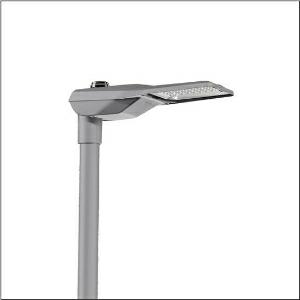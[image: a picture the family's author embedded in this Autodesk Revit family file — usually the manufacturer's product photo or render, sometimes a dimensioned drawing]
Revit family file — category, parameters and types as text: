
# Revit family: streetlight_sl_21_mini___p0_8a_5xe6u47n08hb_863c
name_source: partatom
category: Lighting Fixtures
units: mm (PartAtom-declared; Revit-internal decimal feet)

## family parameters
Cut with Voids When Loaded = No
Host = Face
Light Source = No
Part Type = Normal
Room Calculation Point = No
Round Connector Dimension = Use Diameter
Shared = No

## types (1)
- --- (1 x LED, 9510 lm, 66 W, 4000K)
    Apparent Load = 66 VA
    CIE Flux Codes = 33 69 96 100 100
    Color Rendering = 70
    Color Temperature = 4000K
    Default Elevation = 1800 mm
    Description = Streetlight SL 21 mini, mast luminaire, primary light control with lens, of PMMA, primary optical cover: cover, of toughened safety glass, transparent, light distribution: P0.8a, light emission: direct distribution, primary light characteristic: asymmetric, installation type: side-entry, LED, 3G 1.5mm², High Power LED, rated luminous flux: 9.510lm, luminous efficacy: 144lm/W, light colour: 740, colour temperature: 4000K, control gear: NEMA (7pin), control: flexible luminous flux parameterisation, time-dependent luminous flux control, constant luminous flux control, pre-setting: linear dimming characteristic, overheat protection, mains connection: 230..240V, AC, 50/60Hz, connection cable pre-assembled, cable length: 8,5m, wiring characteristics: H07RN-F, start of lifetime: 66W, end of service life: 69W, reduction: 30W, luminaire housing, of diecast aluminium (EN AC-44300), powder-coated, Siteco® metallic grey (DB 702S), corrosivity category C5 mid according to DIN EN ISO 12944, multi-level sealing system, sealing non-destructively replaceable, inclination adjustable: 0°, 5°, 10°, 15°, length: 628mm, width: 235mm, height: 110mm, spigot size: 42mm (side-entry), mounting height: 4..8m, protection rating (complete): IP66, insulation class (complete): insulation class I (protective earthing), certification: CE, ENEC, ENEC+, VDE, impact resistance: IK10, permissible operating ambient temperature for outdoor applications: -40..+50°C, standard-compliant lighting for roads and squares, packaging unit: 1 piece

Light Distribution: P0.8a
    Height = 110 mm
    Lamp = 1 x LED
    Lamp Light Flux = 9510 lm
    Lamp Power = 66 W
    Lamp count = 1
    Length = 625 mm
    Luminous efficacy = 144 lm/W
    Manufacturer = Siteco
    ModVariant = No
    Model = 5XE6U47N08HB
    Number of Poles = 1
    OnlyDefault = Yes
    Power Factor = 1
    Product Name = Streetlight SL 21 mini | P0.8a
    Product group = mast luminaire | pylon top
    ProductGroupID = 6100
    Protection Class = Protection class I
    Protection Degree = IP 66
    RLX_Detail_Level = 1
    RLX_Emergency_Light_Flux = 0 lm
    RLX_Emergency_Type = 0
    RLX_Emergency_Type_DB = No
    RlxData = <blob elided: 25869 chars, md5=6b50883a>
    Socket = socket
    Standby Power = 0 W
    System Light Flux = 9510 lm
    System Power = 66 W
    Type Comments = factory setting: luminous flux: 100 % | dim-lin: 254 | 670 mA
    Type Image = l_1294379.jpg
    URL = http://relux.com
    VarID = @adj_073504
    Voltage = 0 V
    Weight = 0.00 kg
    Width = 234 mm

## geometry (parser evidence)
native form markers: Blend x4, Sweep x12
no freeform markers — native parametric forms only
